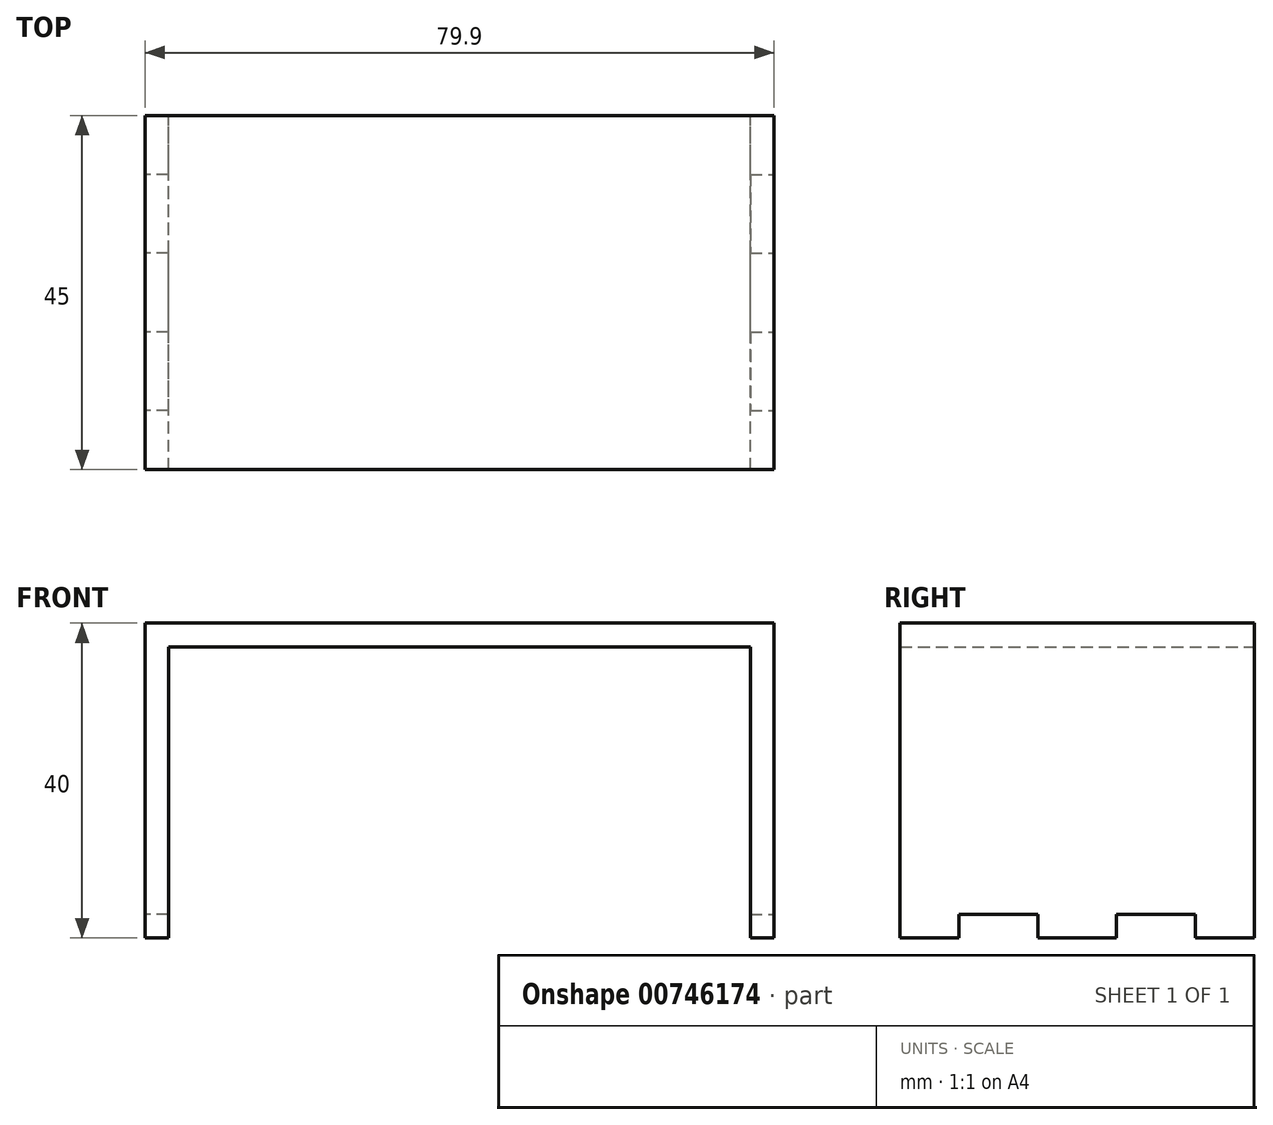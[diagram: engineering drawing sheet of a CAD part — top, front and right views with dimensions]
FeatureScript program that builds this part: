
annotation { "Feature Type Name" : "Feature", "Feature Type Description" : "" }
export const myFeature = defineFeature(function(context is Context, id is Id, definition is map)
    precondition{}
    {
        {
            var Q0;
            Q0=qCreatedBy(makeId("Front.planeOp"),FACE);
            var sketch = newSketch(context, id + "F0", { "sketchPlane" : qUnion([Q0])});
            skLineSegment(sketch, "E0", {"start": v(0, 3) * mm, "end": v(79.9, 3) * mm});
            skLineSegment(sketch, "E1", {"start": v(79.9, 3) * mm, "end": v(79.9, -37) * mm});
            skLineSegment(sketch, "E2", {"start": v(79.9, -37) * mm, "end": v(76.9, -37) * mm});
            skLineSegment(sketch, "E3", {"start": v(76.9, -37) * mm, "end": v(76.9, 0) * mm});
            skLineSegment(sketch, "E4", {"start": v(76.9, 0) * mm, "end": v(3, 0) * mm});
            skLineSegment(sketch, "E5", {"start": v(3, 0) * mm, "end": v(3, -37) * mm});
            skLineSegment(sketch, "E6", {"start": v(3, -37) * mm, "end": v(0, -37) * mm});
            skLineSegment(sketch, "E7", {"start": v(0, 3) * mm, "end": v(0, -37) * mm});
            skSolve(sketch);
        }
        {
            var Q0;
            Q0 = qSketchRegion(id + "F0", true);
            extrude(context, id + "F1", {"entities" : qUnion([Q0]), "depth" : 45 * mm, "offsetDistance" : 25 * mm});
        }
        {
            var Q0;
            Q0=makeQuery(id+"F1.opExtrude","SWEPT_FACE",FACE,{"disambiguationData":[OSD([sQuery(id+"F0.wireOp",EDGE,"E1")])]});
            var sketch = newSketch(context, id + "F2", { "sketchPlane" : qUnion([Q0])});
            skLineSegment(sketch, "E8", {"start": v(-37.5, -37) * mm, "end": v(-37.5, -34) * mm});
            skLineSegment(sketch, "E9", {"start": v(-37.5, -34) * mm, "end": v(-27.5, -34) * mm});
            skLineSegment(sketch, "E10", {"start": v(-27.5, -34) * mm, "end": v(-27.5, -37) * mm});
            skLineSegment(sketch, "E11", {"start": v(-17.5, -37) * mm, "end": v(-17.5, -34) * mm});
            skLineSegment(sketch, "E12", {"start": v(-17.5, -34) * mm, "end": v(-7.5, -34) * mm});
            skLineSegment(sketch, "E13", {"start": v(-7.5, -34) * mm, "end": v(-7.5, -37) * mm});
            skSolve(sketch);
        }
        {
            var Q0;
            Q0 = qSketchRegion(id + "F2", true);
            var Q1;
            {var subQ0=sQuery(id+"F2.wireOp",EDGE,"E8");Q1=makeQuery(id+"F2.imprint","IMPRINT",FACE,{"disambiguationData":[TD([[makeQuery(id+"F2.imprint","IMPRINT",EDGE,{"derivedFrom":subQ0}),-1.0]])]});}
            var Q2;
            {var subQ0=sQuery(id+"F2.wireOp",EDGE,"E11");Q2=makeQuery(id+"F2.imprint","IMPRINT",FACE,{"disambiguationData":[TD([[makeQuery(id+"F2.imprint","IMPRINT",EDGE,{"derivedFrom":subQ0}),-1.0]])]});}
            extrude(context, id + "F3", {"entities" : qUnion([Q0, Q1, Q2]), "operationType" : NewBodyOperationType.REMOVE, "oppositeDirection" : true, "depth" : 25 * mm, "offsetDistance" : 25 * mm});
        }
        {
            var Q0;
            Q0=makeQuery(id+"F1.opExtrude","SWEPT_FACE",FACE,{"disambiguationData":[OSD([sQuery(id+"F0.wireOp",EDGE,"E7")])]});
            var sketch = newSketch(context, id + "F4", { "sketchPlane" : qUnion([Q0])});
            skLineSegment(sketch, "E14", {"start": v(7.5, -37) * mm, "end": v(7.5, -34) * mm});
            skLineSegment(sketch, "E15", {"start": v(7.5, -34) * mm, "end": v(17.5, -34) * mm});
            skLineSegment(sketch, "E16", {"start": v(17.5, -34) * mm, "end": v(17.5, -37) * mm});
            skLineSegment(sketch, "E17", {"start": v(27.5, -37) * mm, "end": v(27.5, -34) * mm});
            skLineSegment(sketch, "E18", {"start": v(27.5, -34) * mm, "end": v(37.5, -34) * mm});
            skLineSegment(sketch, "E19", {"start": v(37.5, -34) * mm, "end": v(37.5, -37) * mm});
            skSolve(sketch);
        }
        {
            var Q0;
            {var subQ0=sQuery(id+"F4.wireOp",EDGE,"E14");Q0=makeQuery(id+"F4.imprint","IMPRINT",FACE,{"disambiguationData":[TD([[makeQuery(id+"F4.imprint","IMPRINT",EDGE,{"derivedFrom":subQ0}),-1.0]])]});}
            var Q1;
            {var subQ0=sQuery(id+"F4.wireOp",EDGE,"E17");Q1=makeQuery(id+"F4.imprint","IMPRINT",FACE,{"disambiguationData":[TD([[makeQuery(id+"F4.imprint","IMPRINT",EDGE,{"derivedFrom":subQ0}),-1.0]])]});}
            extrude(context, id + "F5", {"entities" : qUnion([Q0, Q1]), "operationType" : NewBodyOperationType.REMOVE, "oppositeDirection" : true, "depth" : 25 * mm, "offsetDistance" : 25 * mm});
        }
    });
